# Revit family: Faucet-Wall_Mount-Lavatory-KOHLER-AVID-K-97359T
name_source: partatom
category: Plumbing Fixtures
revit_build: Autodesk Revit 2017 (Build: 20160225_1515(x64)
units: mm (PartAtom-declared; Revit-internal decimal feet)

## family parameters
Cut with Voids When Loaded = No
Host = Face
OmniClass Number = 23.31.11.00
OmniClass Title = Faucets
Part Type = Normal
Room Calculation Point = No
Round Connector Dimension = Use Diameter
Shared = No

## types (5) — shared parameters
ADA Compliant = No
Assembly Code = D2010
CW Connection = Yes
Cold Water Inlet = Cold Water Inlet
Date Modified = 12/23/2021
Default Elevation = 36"
Drain Included = Yes
Faucet Hole Spacing = 7 15/16"
Flow Rate = 2 GPM
HW Connection = Yes
Handle Clearance = 3"
Height = 2 1/16"
Hot Water Inlet = Hot Water Inlet
Length = 8 1/4"
Manufacturer = KOHLER Co.
Master Format 2014 = 22 41 39
Master Format 2014 Name = Residential Faucets, Supplies, and Trim
Material = Premium Metal Construction
Product Name = AVID
Spout Reach = 8 1/4"
URL = http://www.kohler.com.cn
Vent Connection = No
Waste Connection = No
Waste Water Outlet = Waste Water Outlet
WaterSense Certified = No
Width = 7 15/16"

## per-type parameters (varying)
| type | Cut Depth | Description | Finish | Model | Pressure | Product Documentation Link | Product Page URL | Type | Valve Included |
| With Valve, 60 PSI, CP-Polished Chrome | 2 11/16" | Ai Fei double handle wall outlet basin faucet | Kohler-Metal-CP-Polished_Chrome | K-97359T-4-CP | 60.00 psi | https://files.kohler.com.cn | https://www.kohler.com.cn | 1 | Yes |
| With Valve, 60 PSI, TT-Titanium Silver | 2 11/16" | Ai Fei double handle wall outlet basin faucet | Kohler-Metal-TT-Titanium_Silver | K-97359T-4-TT | 60.00 psi | https://files.kohler.com.cn | https://www.kohler.com.cn | 2 | Yes |
| Without Valve, 45 PSI, CP-Polished Chrome | 0" | DUAL HANDLE WALL MOUNT LAVATORY FAUCET WITHOUT VALVE | Kohler-Metal-CP-Polished_Chrome | K-97359T-B4-CP | 45.00 psi |  |  | 3 | No |
| Without Valve, 45 PSI, RGD-Rose Gold | 0" | DUAL HANDLE WALL MOUNT LAVATORY FAUCET WITHOUT VALVE | Kohler-Metal-RGD-Rose_Gold | K-97359T-B4-RGD | 45.00 psi |  |  | 4 | No |
| Without Valve, 45 PSI, TT-Titanium Silver | 0" | DUAL HANDLE WALL MOUNT LAVATORY FAUCET WITHOUT VALVE | Kohler-Metal-TT-Titanium_Silver | K-97359T-B4-TT | 45.00 psi |  |  | 5 | No |

## geometry (parser evidence)
native form markers: Sweep x11
no freeform markers — native parametric forms only
